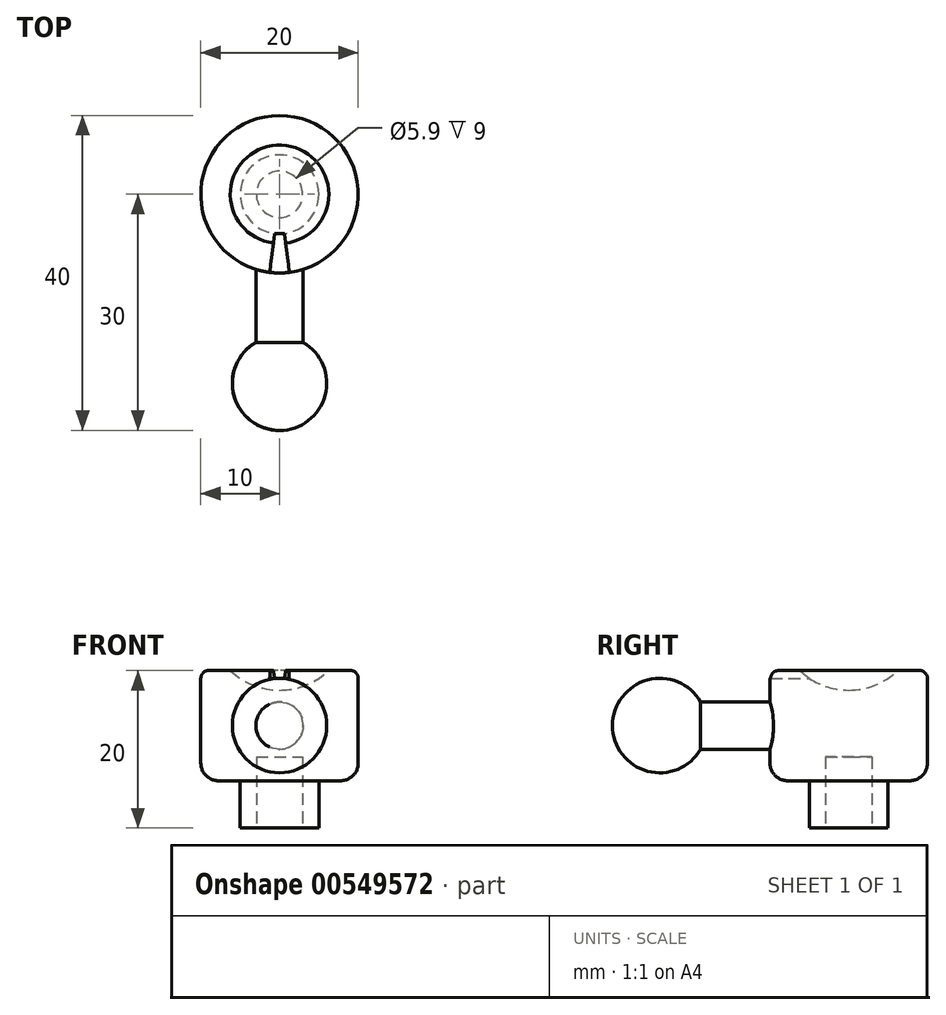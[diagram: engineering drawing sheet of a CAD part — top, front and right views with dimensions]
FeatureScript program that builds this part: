
annotation { "Feature Type Name" : "Feature", "Feature Type Description" : "" }
export const myFeature = defineFeature(function(context is Context, id is Id, definition is map)
    precondition{}
    {
        {
            var Q0;
            Q0=qCreatedBy(makeId("Top.planeOp"),FACE);
            var sketch = newSketch(context, id + "F0", { "sketchPlane" : qUnion([Q0])});
            skCircle(sketch, "E0", {"center": v(0, 0) * mm, "radius": 10 * mm});
            skSolve(sketch);
        }
        {
            var Q0;
            Q0 = qSketchRegion(id + "F0", true);
            extrude(context, id + "F1", {"entities" : qUnion([Q0]), "endBound" : BoundingType.SYMMETRIC, "depth" : 14 * mm, "offsetDistance" : 25 * mm, "hasSecondDirection" : true, "secondDirectionOppositeDirection" : true, "secondDirectionDepth" : 8 * mm});
        }
        {
            var Q0;
            Q0=makeQuery(id+"F1.opExtrude","CAP_FACE",FACE,{"disambiguationData":[OSD([sQuery(id+"F0.wireOp",EDGE,"E0")])],"isStart":true});
            var sketch = newSketch(context, id + "F2", { "sketchPlane" : qUnion([Q0])});
            skCircle(sketch, "E1", {"center": v(0, 0) * mm, "radius": 5 * mm});
            skSolve(sketch);
        }
        {
            var Q0;
            Q0 = qSketchRegion(id + "F2", true);
            extrude(context, id + "F3", {"entities" : qUnion([Q0]), "operationType" : NewBodyOperationType.ADD, "depth" : 6 * mm, "offsetDistance" : 25 * mm});
        }
        {
            var Q0;
            Q0=makeQuery(id+"F3.opExtrude","CAP_FACE",FACE,{"disambiguationData":[OSD([sQuery(id+"F2.wireOp",EDGE,"E1")])],"isStart":false});
            var sketch = newSketch(context, id + "F4", { "sketchPlane" : qUnion([Q0])});
            skCircle(sketch, "E2", {"center": v(0, 0) * mm, "radius": 2.95 * mm});
            skSolve(sketch);
        }
        {
            var Q0;
            Q0 = qSketchRegion(id + "F4", true);
            extrude(context, id + "F5", {"entities" : qUnion([Q0]), "operationType" : NewBodyOperationType.REMOVE, "oppositeDirection" : true, "depth" : 9 * mm, "offsetDistance" : 25 * mm});
        }
        {
            var Q0;
            Q0=qCreatedBy(makeId("Top.planeOp"),FACE);
            var sketch = newSketch(context, id + "F6", { "sketchPlane" : qUnion([Q0])});
            skLineSegment(sketch, "E3", {"start": v(0, 0) * mm, "end": v(0, -46.52) * mm, "construction": true});
            skLineSegment(sketch, "E4", {"start": v(0, -9.54) * mm, "end": v(-3, -9.54) * mm});
            skLineSegment(sketch, "E5", {"start": v(-3, -9.54) * mm, "end": v(-3, -18.8) * mm});
            skArc(sketch, "E6", {"start": v(-3, -18.8) * mm, "mid": v(-5.8, -25.55) * mm, "end": v(0, -30) * mm});
            skLineSegment(sketch, "E7", {"start": v(0, -9.54) * mm, "end": v(0, -30) * mm});
            skSolve(sketch);
        }
        {
            var Q0;
            Q0 = qSketchRegion(id + "F6", true);
            var Q1;
            Q1=sQuery(id+"F6.wireOp",EDGE,"E3");
            revolve(context, id + "F7", {"operationType" : NewBodyOperationType.ADD, "entities" : qUnion([Q0]), "axis" : qUnion([Q1]), "revolveType" : RevolveType.FULL});
        }
        {
            var Q0;
            Q0=makeQuery(id+"F1.opExtrude","CAP_FACE",FACE,{"disambiguationData":[OSD([sQuery(id+"F0.wireOp",EDGE,"E0")])],"isStart":false});
            var sketch = newSketch(context, id + "F8", { "sketchPlane" : qUnion([Q0])});
            skLineSegment(sketch, "E8", {"start": v(0, 0) * mm, "end": v(0, -13.9) * mm, "construction": true});
            skLineSegment(sketch, "E9", {"start": v(-1.25, -10) * mm, "end": v(-0.62, -5) * mm});
            skLineSegment(sketch, "E10", {"start": v(-0.62, -5) * mm, "end": v(0.62, -5) * mm});
            skLineSegment(sketch, "E11", {"start": v(0.62, -5) * mm, "end": v(1.25, -10) * mm});
            skLineSegment(sketch, "E12", {"start": v(1.25, -10) * mm, "end": v(-1.25, -10) * mm});
            skPoint(sketch, "E13", {"position": v(0, -10) * mm});
            skSolve(sketch);
        }
        {
            var Q0;
            Q0 = qSketchRegion(id + "F8", true);
            extrude(context, id + "F9", {"entities" : qUnion([Q0]), "operationType" : NewBodyOperationType.REMOVE, "oppositeDirection" : true, "depth" : 1 * mm, "offsetDistance" : 25 * mm});
        }
        {
            var Q0;
            Q0=qCreatedBy(makeId("Front.planeOp"),FACE);
            var sketch = newSketch(context, id + "F10", { "sketchPlane" : qUnion([Q0])});
            skArc(sketch, "E14", {"start": v(0, 4.5) * mm, "mid": v(3.7, 5.28) * mm, "end": v(6.75, 7.5) * mm});
            skLineSegment(sketch, "E15", {"start": v(0, 4.5) * mm, "end": v(0, 13.58) * mm});
            skPoint(sketch, "E16", {"position": v(5, 6) * mm});
            skLineSegment(sketch, "E17.0", {"start": v(5, 6) * mm, "end": v(9.92, 6) * mm, "construction": true});
            skArc(sketch, "E18", {"start": v(10, 6) * mm, "mid": v(9.7, 6.7) * mm, "end": v(9, 7) * mm});
            skLineSegment(sketch, "E19", {"start": v(10, 6) * mm, "end": v(12.88, 6) * mm});
            skLineSegment(sketch, "E20", {"start": v(12.88, 6) * mm, "end": v(0, 13.58) * mm});
            skLineSegment(sketch, "E21", {"start": v(9, 7) * mm, "end": v(9, 7.5) * mm});
            skLineSegment(sketch, "E22", {"start": v(9, 7.5) * mm, "end": v(6.75, 7.5) * mm});
            skSolve(sketch);
        }
        {
            var Q0;
            Q0 = qSketchRegion(id + "F10", true);
            var Q1;
            Q1=sQuery(id+"F10.wireOp",EDGE,"E15");
            revolve(context, id + "F11", {"operationType" : NewBodyOperationType.REMOVE, "entities" : qUnion([Q0]), "axis" : qUnion([Q1]), "revolveType" : RevolveType.FULL, "oppositeDirection" : true});
        }
        {
            var Q0;
            Q0=makeQuery(id+"F1.opExtrude","CAP_EDGE",EDGE,{"disambiguationData":[OSD([sQuery(id+"F0.wireOp",EDGE,"E0")])],"isStart":true});
            var Q1;
            Q1=makeQuery(id+"F3.opExtrude","CAP_EDGE",EDGE,{"disambiguationData":[OSD([sQuery(id+"F2.wireOp",EDGE,"E1")])],"isStart":true});
            fillet(context, id + "F12", {"entities" : qUnion([Q0, Q1]), "radius" : 2.25 * mm, "tangentPropagation" : true, "allowEdgeOverflow" : false});
        }
    });
